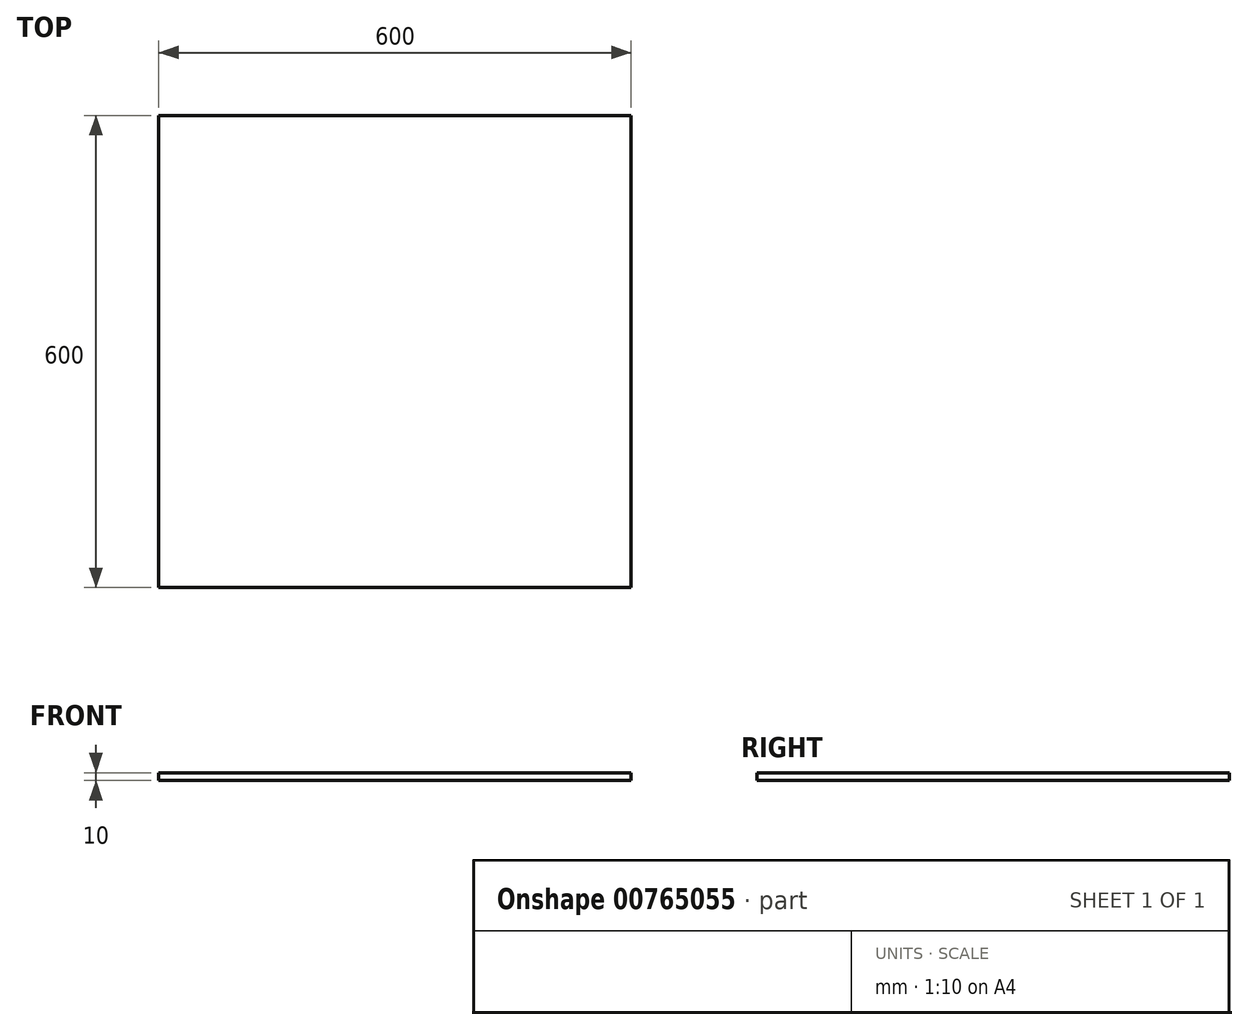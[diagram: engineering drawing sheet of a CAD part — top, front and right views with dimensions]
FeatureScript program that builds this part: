
annotation { "Feature Type Name" : "Feature", "Feature Type Description" : "" }
export const myFeature = defineFeature(function(context is Context, id is Id, definition is map)
    precondition{}
    {
        {
            var Q0;
            Q0=qCreatedBy(makeId("Top.planeOp"),FACE);
            var sketch = newSketch(context, id + "F0", { "sketchPlane" : qUnion([Q0])});
            skLineSegment(sketch, "E0.bottom", {"start": v(0, 0) * mm, "end": v(600, 0) * mm});
            skLineSegment(sketch, "E0.top", {"start": v(0, 600) * mm, "end": v(600, 600) * mm});
            skLineSegment(sketch, "E0.left", {"start": v(0, 0) * mm, "end": v(0, 600) * mm});
            skLineSegment(sketch, "E0.right", {"start": v(600, 0) * mm, "end": v(600, 600) * mm});
            skSolve(sketch);
        }
        {
            var Q0;
            Q0 = qSketchRegion(id + "F0", true);
            extrude(context, id + "F1", {"entities" : qUnion([Q0]), "depth" : 10 * mm, "offsetDistance" : 25 * mm});
        }
    });
